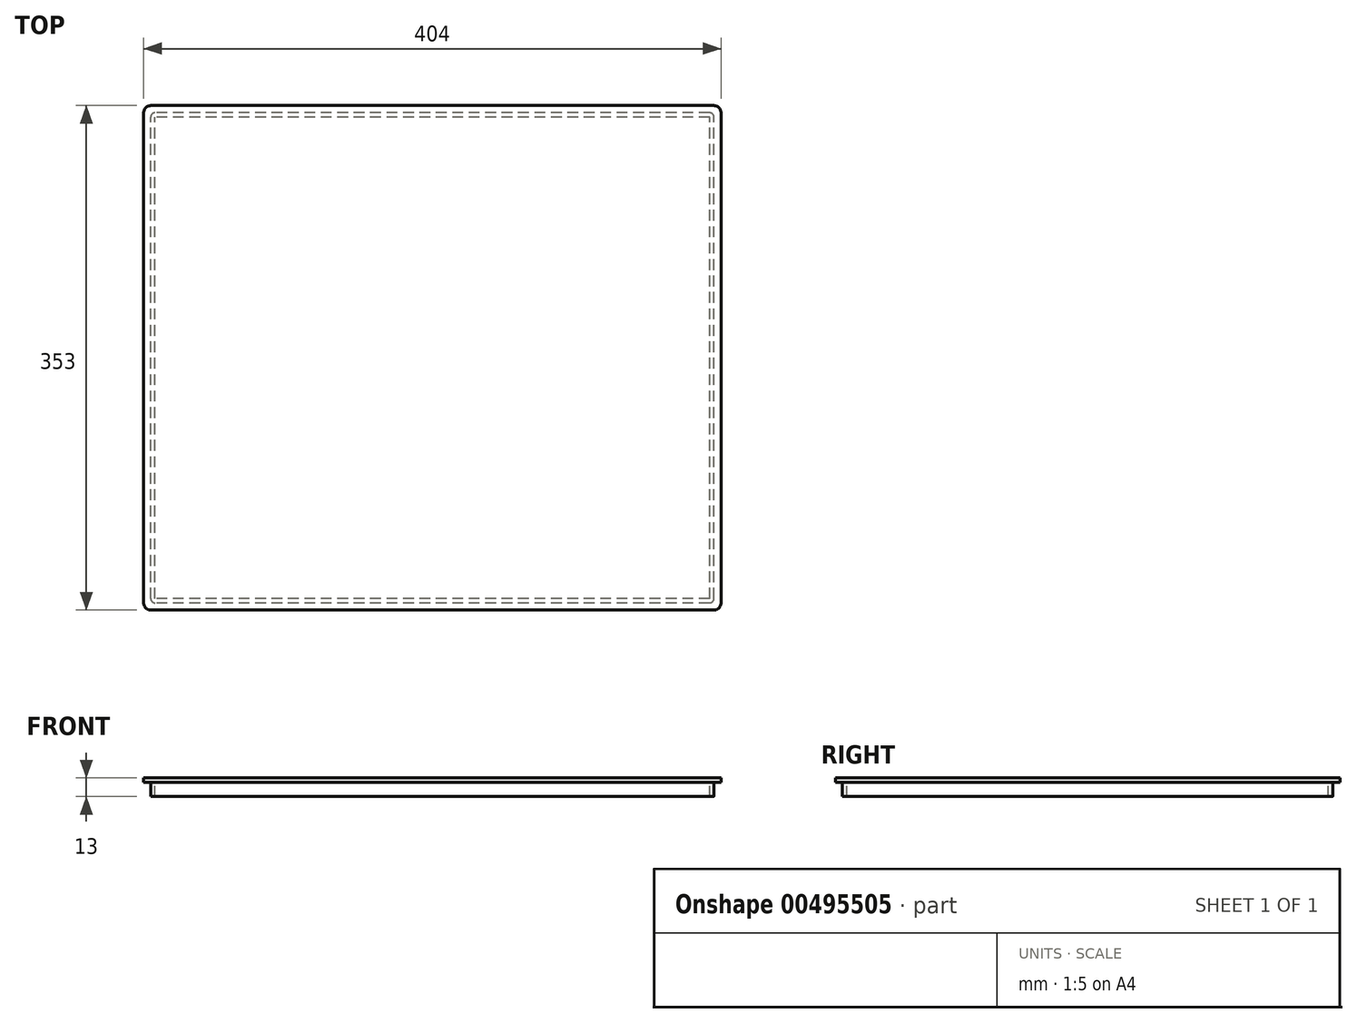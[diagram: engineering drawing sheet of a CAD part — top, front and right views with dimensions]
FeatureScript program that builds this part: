
annotation { "Feature Type Name" : "Feature", "Feature Type Description" : "" }
export const myFeature = defineFeature(function(context is Context, id is Id, definition is map)
    precondition{}
    {
        {
            var Q0;
            Q0=qCreatedBy(makeId("Top.planeOp"),FACE);
            var sketch = newSketch(context, id + "F0", { "sketchPlane" : qUnion([Q0])});
            skLineSegment(sketch, "E0.bottom", {"start": v(197, -171.5) * mm, "end": v(-197, -171.5) * mm});
            skLineSegment(sketch, "E0.top", {"start": v(197, 171.5) * mm, "end": v(-197, 171.5) * mm});
            skLineSegment(sketch, "E0.left", {"start": v(197, -171.5) * mm, "end": v(197, 171.5) * mm});
            skLineSegment(sketch, "E0.right", {"start": v(-197, -171.5) * mm, "end": v(-197, 171.5) * mm});
            skPoint(sketch, "E0.middle", {"position": v(0, 0) * mm});
            skLineSegment(sketch, "E1.0", {"start": v(194, 168.5) * mm, "end": v(-194, 168.5) * mm});
            skLineSegment(sketch, "E1.1", {"start": v(194, -168.5) * mm, "end": v(194, 168.5) * mm});
            skLineSegment(sketch, "E1.2", {"start": v(194, -168.5) * mm, "end": v(-194, -168.5) * mm});
            skLineSegment(sketch, "E1.3", {"start": v(-194, -168.5) * mm, "end": v(-194, 168.5) * mm});
            skSolve(sketch);
        }
        {
            var Q0;
            Q0 = qSketchRegion(id + "F0", true);
            extrude(context, id + "F1", {"entities" : qUnion([Q0]), "oppositeDirection" : true, "depth" : 10 * mm});
        }
        {
            var Q0;
            Q0=makeQuery(id+"F1.opExtrude","CAP_FACE",FACE,{"disambiguationData":[OSD([sQuery(id+"F0.wireOp",EDGE,"E0.bottom"),sQuery(id+"F0.wireOp",EDGE,"E0.top"),sQuery(id+"F0.wireOp",EDGE,"E0.left"),sQuery(id+"F0.wireOp",EDGE,"E0.right"),sQuery(id+"F0.wireOp",EDGE,"E1.0"),sQuery(id+"F0.wireOp",EDGE,"E1.1"),sQuery(id+"F0.wireOp",EDGE,"E1.2"),sQuery(id+"F0.wireOp",EDGE,"E1.3")])],"isStart":true});
            var sketch = newSketch(context, id + "F2", { "sketchPlane" : qUnion([Q0])});
            skLineSegment(sketch, "E2.bottom", {"start": v(202, -176.5) * mm, "end": v(-202, -176.5) * mm});
            skLineSegment(sketch, "E2.top", {"start": v(202, 176.5) * mm, "end": v(-202, 176.5) * mm});
            skLineSegment(sketch, "E2.left", {"start": v(202, -176.5) * mm, "end": v(202, 176.5) * mm});
            skLineSegment(sketch, "E2.right", {"start": v(-202, -176.5) * mm, "end": v(-202, 176.5) * mm});
            skPoint(sketch, "E2.middle", {"position": v(0, 0) * mm});
            skSolve(sketch);
        }
        {
            var Q0;
            Q0 = qSketchRegion(id + "F2", true);
            extrude(context, id + "F3", {"entities" : qUnion([Q0]), "operationType" : NewBodyOperationType.ADD, "depth" : 3 * mm});
        }
        {
            var Q0;
            Q0=makeQuery(id+"F3.opExtrude","SWEPT_EDGE",EDGE,{"disambiguationData":[OSD([sQuery(id+"F2.wireOp",EDGE,"E2.bottom"),sQuery(id+"F2.wireOp",EDGE,"E2.right")])]});
            var Q1;
            Q1=makeQuery(id+"F3.opExtrude","SWEPT_EDGE",EDGE,{"disambiguationData":[OSD([sQuery(id+"F2.wireOp",EDGE,"E2.bottom"),sQuery(id+"F2.wireOp",EDGE,"E2.left")])]});
            var Q2;
            Q2=makeQuery(id+"F3.opExtrude","SWEPT_EDGE",EDGE,{"disambiguationData":[OSD([sQuery(id+"F2.wireOp",EDGE,"E2.top"),sQuery(id+"F2.wireOp",EDGE,"E2.left")])]});
            var Q3;
            Q3=makeQuery(id+"F3.opExtrude","SWEPT_EDGE",EDGE,{"disambiguationData":[OSD([sQuery(id+"F2.wireOp",EDGE,"E2.top"),sQuery(id+"F2.wireOp",EDGE,"E2.right")])]});
            fillet(context, id + "F4", {"entities" : qUnion([Q0, Q1, Q2, Q3]), "radius" : 5 * mm, "tangentPropagation" : true, "allowEdgeOverflow" : false});
        }
        {
            var Q0;
            Q0=makeQuery(id+"F1.opExtrude","SWEPT_EDGE",EDGE,{"disambiguationData":[OSD([sQuery(id+"F0.wireOp",EDGE,"E0.top"),sQuery(id+"F0.wireOp",EDGE,"E0.left")])]});
            var Q1;
            Q1=makeQuery(id+"F1.opExtrude","SWEPT_EDGE",EDGE,{"disambiguationData":[OSD([sQuery(id+"F0.wireOp",EDGE,"E0.top"),sQuery(id+"F0.wireOp",EDGE,"E0.right")])]});
            var Q2;
            Q2=makeQuery(id+"F1.opExtrude","SWEPT_EDGE",EDGE,{"disambiguationData":[OSD([sQuery(id+"F0.wireOp",EDGE,"E0.bottom"),sQuery(id+"F0.wireOp",EDGE,"E0.right")])]});
            var Q3;
            Q3=makeQuery(id+"F1.opExtrude","SWEPT_EDGE",EDGE,{"disambiguationData":[OSD([sQuery(id+"F0.wireOp",EDGE,"E0.bottom"),sQuery(id+"F0.wireOp",EDGE,"E0.left")])]});
            fillet(context, id + "F5", {"entities" : qUnion([Q0, Q1, Q2, Q3]), "radius" : 3 * mm, "tangentPropagation" : true, "allowEdgeOverflow" : false});
        }
    });
